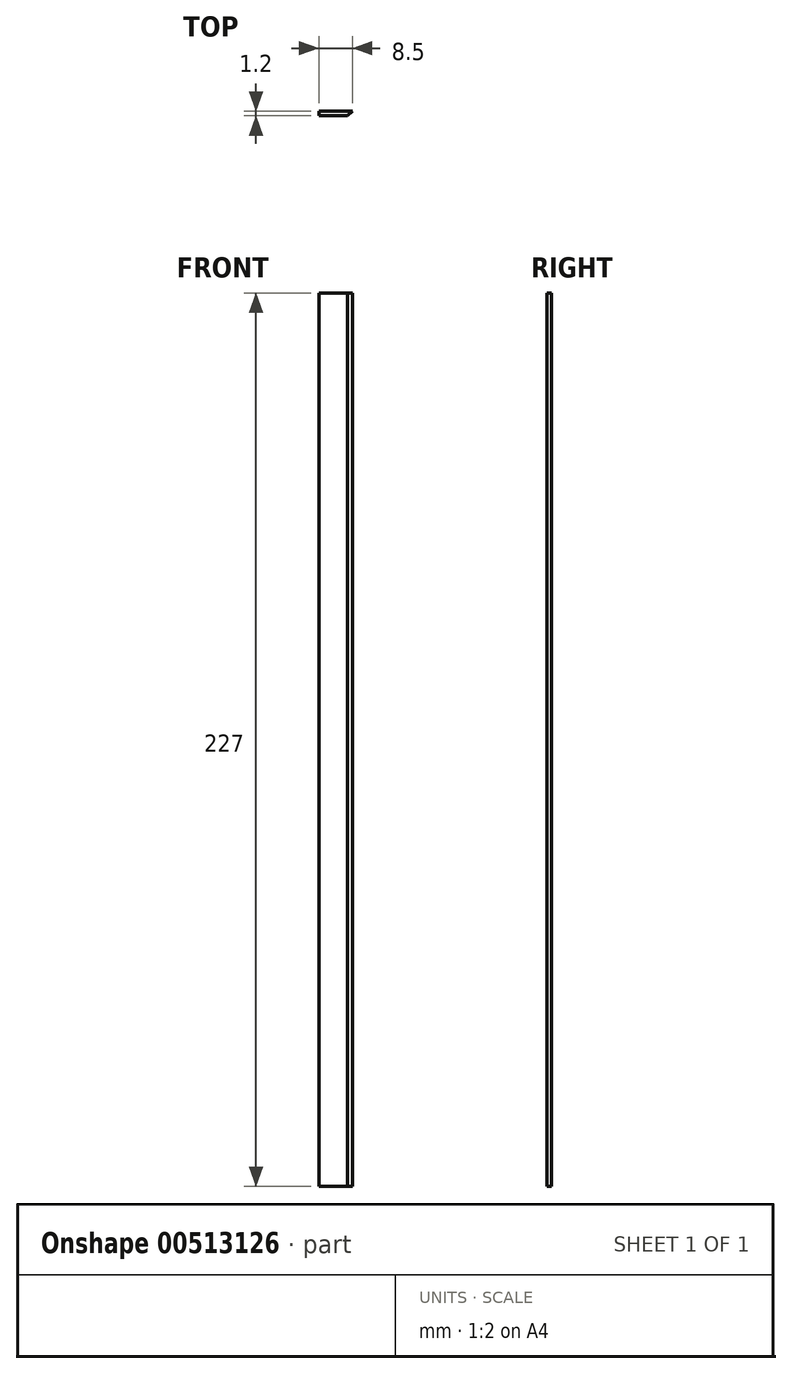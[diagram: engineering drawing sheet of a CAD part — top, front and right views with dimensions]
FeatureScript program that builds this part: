
annotation { "Feature Type Name" : "Feature", "Feature Type Description" : "" }
export const myFeature = defineFeature(function(context is Context, id is Id, definition is map)
    precondition{}
    {
        {
            var Q0;
            Q0=qCreatedBy(makeId("Top.planeOp"),FACE);
            var sketch = newSketch(context, id + "F0", { "sketchPlane" : qUnion([Q0])});
            skLineSegment(sketch, "E0", {"start": v(-36.36, 9.11) * mm, "end": v(-36.36, 7.91) * mm});
            skLineSegment(sketch, "E1", {"start": v(-29.06, 7.91) * mm, "end": v(-36.36, 7.91) * mm});
            skLineSegment(sketch, "E2", {"start": v(-36.36, 9.11) * mm, "end": v(-27.86, 9.11) * mm});
            skLineSegment(sketch, "E3", {"start": v(-29.06, 7.91) * mm, "end": v(-27.86, 9.11) * mm});
            skSolve(sketch);
        }
        {
            var Q0;
            Q0=makeQuery(id+"F0.imprint","IMPRINT",FACE,{"disambiguationData":[TD([[makeQuery(id+"F0.imprint","IMPRINT",EDGE,{"derivedFrom":sQuery(id+"F0.wireOp",EDGE,"E0")}),1.0]])]});
            extrude(context, id + "F1", {"entities" : qUnion([Q0]), "depth" : 227 * mm});
        }
    });
